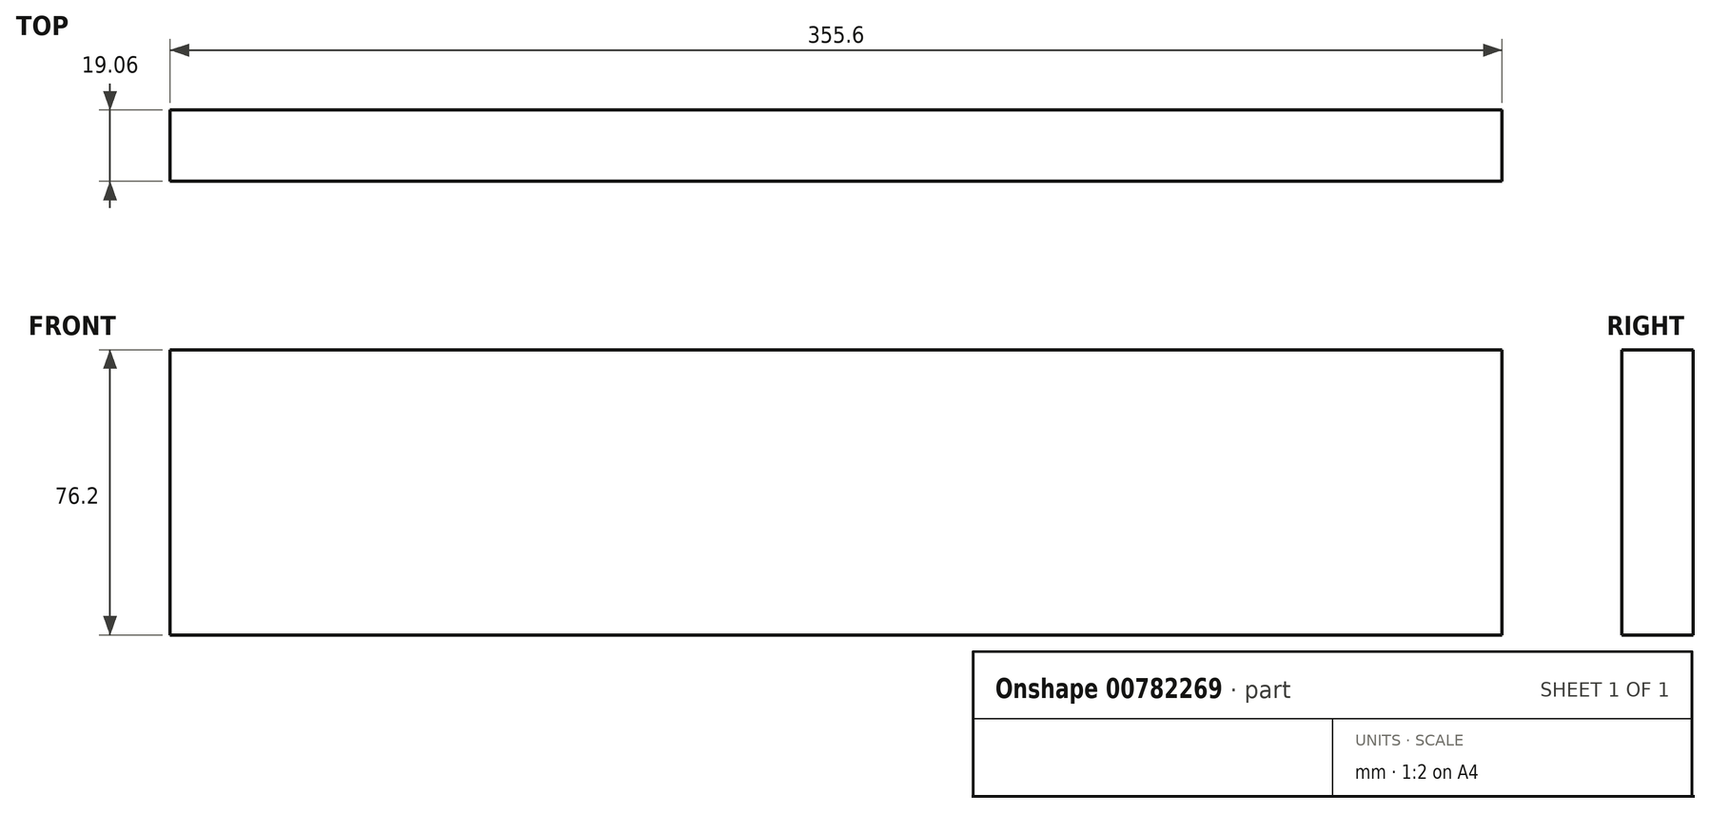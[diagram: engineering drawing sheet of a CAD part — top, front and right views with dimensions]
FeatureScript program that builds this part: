
annotation { "Feature Type Name" : "Feature", "Feature Type Description" : "" }
export const myFeature = defineFeature(function(context is Context, id is Id, definition is map)
    precondition{}
    {
        {
            var Q0;
            Q0=qCreatedBy(makeId("Front.planeOp"),FACE);
            var sketch = newSketch(context, id + "F0", { "sketchPlane" : qUnion([Q0])});
            skLineSegment(sketch, "E0.bottom", {"start": v(-177.8, 38.1) * mm, "end": v(177.8, 38.1) * mm});
            skLineSegment(sketch, "E0.top", {"start": v(-177.8, -38.1) * mm, "end": v(177.8, -38.1) * mm});
            skLineSegment(sketch, "E0.left", {"start": v(-177.8, 38.1) * mm, "end": v(-177.8, -38.1) * mm});
            skLineSegment(sketch, "E0.right", {"start": v(177.8, 38.1) * mm, "end": v(177.8, -38.1) * mm});
            skLineSegment(sketch, "E1", {"start": v(-177.8, 38.1) * mm, "end": v(177.8, -38.1) * mm, "construction": true});
            skSolve(sketch);
        }
        {
            var Q0;
            Q0 = qSketchRegion(id + "F0", true);
            extrude(context, id + "F1", {"entities" : qUnion([Q0]), "endBound" : BoundingType.SYMMETRIC, "depth" : 19.05 * mm, "offsetDistance" : 25.4 * mm});
        }
    });
